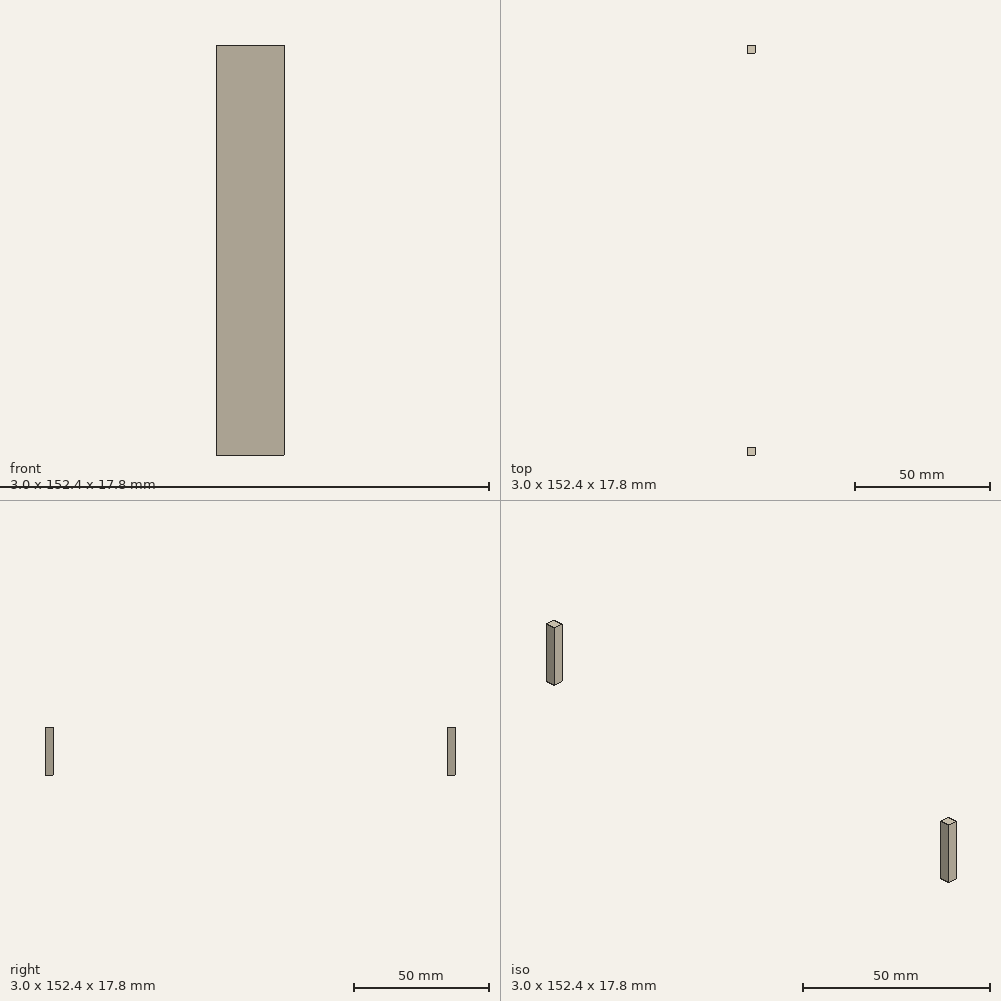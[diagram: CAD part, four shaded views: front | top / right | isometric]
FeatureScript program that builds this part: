
annotation { "Feature Type Name" : "Feature", "Feature Type Description" : "" }
export const myFeature = defineFeature(function(context is Context, id is Id, definition is map)
    precondition{}
    {
        {
            var Q0;
            Q0=qCreatedBy(makeId("Right.planeOp"),FACE);
            var sketch = newSketch(context, id + "F0", { "sketchPlane" : qUnion([Q0])});
            skLineSegment(sketch, "E0.bottom", {"start": v(76.2, -34.3) * mm, "end": v(-76.2, -34.3) * mm});
            skLineSegment(sketch, "E0.top", {"start": v(76.2, 34.3) * mm, "end": v(-76.2, 34.3) * mm});
            skLineSegment(sketch, "E0.left", {"start": v(76.2, -34.3) * mm, "end": v(76.2, 34.3) * mm});
            skLineSegment(sketch, "E0.right", {"start": v(-76.2, -34.3) * mm, "end": v(-76.2, 34.3) * mm});
            skPoint(sketch, "E0.middle", {"position": v(0, 0) * mm});
            skLineSegment(sketch, "E1.bottom", {"start": v(-76.2, -8.9) * mm, "end": v(-73.23, -8.9) * mm});
            skLineSegment(sketch, "E1.top", {"start": v(-76.2, -34.3) * mm, "end": v(-73.23, -34.3) * mm});
            skLineSegment(sketch, "E1.left", {"start": v(-76.2, -8.9) * mm, "end": v(-76.2, -34.3) * mm});
            skLineSegment(sketch, "E1.right", {"start": v(-73.23, -8.9) * mm, "end": v(-73.23, -34.3) * mm});
            skArc(sketch, "E2", {"start": v(-76.2, 2.57) * mm, "mid": v(-73.15, 3.8) * mm, "end": v(-76.2, 5.05) * mm});
            skLineSegment(sketch, "E3.bottom", {"start": v(-73.23, 34.3) * mm, "end": v(-76.2, 34.3) * mm});
            skLineSegment(sketch, "E3.top", {"start": v(-73.23, 16.51) * mm, "end": v(-76.2, 16.51) * mm});
            skLineSegment(sketch, "E3.left", {"start": v(-73.23, 34.3) * mm, "end": v(-73.23, 16.51) * mm});
            skLineSegment(sketch, "E3.right", {"start": v(-76.2, 34.3) * mm, "end": v(-76.2, 16.51) * mm});
            skLineSegment(sketch, "E4.MirrorCS", {"start": v(76.2, -34.3) * mm, "end": v(73.23, -34.3) * mm});
            skLineSegment(sketch, "E5.MirrorCS", {"start": v(73.23, 34.3) * mm, "end": v(76.2, 34.3) * mm});
            skLineSegment(sketch, "E6.MirrorCS", {"start": v(76.2, -8.9) * mm, "end": v(73.23, -8.9) * mm});
            skLineSegment(sketch, "E7.MirrorCS", {"start": v(73.23, 16.51) * mm, "end": v(76.2, 16.51) * mm});
            skArc(sketch, "E8.MirrorCS", {"start": v(76.2, 2.57) * mm, "mid": v(73.15, 3.8) * mm, "end": v(76.2, 5.05) * mm});
            skLineSegment(sketch, "E9.MirrorCS", {"start": v(73.23, -8.9) * mm, "end": v(73.23, -34.3) * mm});
            skLineSegment(sketch, "E10.MirrorCS", {"start": v(76.2, -8.9) * mm, "end": v(76.2, -34.3) * mm});
            skLineSegment(sketch, "E11.MirrorCS", {"start": v(76.2, 34.3) * mm, "end": v(76.2, 16.51) * mm});
            skLineSegment(sketch, "E12.MirrorCS", {"start": v(73.23, 34.3) * mm, "end": v(73.23, 16.51) * mm});
            skLineSegment(sketch, "E13.bottom", {"start": v(-76.2, -31.32) * mm, "end": v(-58.92, -31.32) * mm});
            skLineSegment(sketch, "E13.top", {"start": v(-76.2, -34.3) * mm, "end": v(-38.1, -34.3) * mm});
            skLineSegment(sketch, "E13.left", {"start": v(-76.2, -31.32) * mm, "end": v(-76.2, -34.3) * mm});
            skLineSegment(sketch, "E13.right", {"start": v(-38.1, -31.32) * mm, "end": v(-38.1, -34.3) * mm});
            skLineSegment(sketch, "E14.bottom", {"start": v(76.2, -31.32) * mm, "end": v(38.1, -31.32) * mm});
            skLineSegment(sketch, "E14.top", {"start": v(76.2, -34.3) * mm, "end": v(38.1, -34.3) * mm});
            skLineSegment(sketch, "E14.left", {"start": v(76.2, -31.32) * mm, "end": v(76.2, -34.3) * mm});
            skLineSegment(sketch, "E14.right", {"start": v(38.1, -31.32) * mm, "end": v(38.1, -34.3) * mm});
            skLineSegment(sketch, "E15.bottom", {"start": v(-12.7, -31.32) * mm, "end": v(12.7, -31.32) * mm});
            skLineSegment(sketch, "E15.top", {"start": v(-12.7, -34.3) * mm, "end": v(12.7, -34.3) * mm});
            skLineSegment(sketch, "E15.left", {"start": v(-12.7, -31.32) * mm, "end": v(-12.7, -34.3) * mm});
            skLineSegment(sketch, "E15.right", {"start": v(12.7, -31.32) * mm, "end": v(12.7, -34.3) * mm});
            skLineSegment(sketch, "E16.bottom", {"start": v(-58.92, -13.49) * mm, "end": v(-55.38, -13.49) * mm});
            skLineSegment(sketch, "E16.top", {"start": v(-58.92, -34.3) * mm, "end": v(-55.38, -34.3) * mm});
            skLineSegment(sketch, "E16.left", {"start": v(-58.92, -13.49) * mm, "end": v(-58.92, -18.52) * mm});
            skLineSegment(sketch, "E16.right", {"start": v(-55.38, -13.49) * mm, "end": v(-55.38, -18.52) * mm});
            skPoint(sketch, "E17", {"position": v(-57.15, -34.3) * mm});
            skLineSegment(sketch, "E18", {"start": v(-57.15, -34.3) * mm, "end": v(-57.15, -8.89) * mm, "construction": true});
            skPoint(sketch, "E18.endSnap0", {"position": v(-57.15, -13.49) * mm});
            skLineSegment(sketch, "E19.bottom", {"start": v(-53.26, -21.16) * mm, "end": v(-55.38, -21.16) * mm});
            skLineSegment(sketch, "E19.top", {"start": v(-53.26, -18.52) * mm, "end": v(-55.38, -18.52) * mm});
            skLineSegment(sketch, "E19.left", {"start": v(-53.26, -21.16) * mm, "end": v(-53.26, -18.52) * mm});
            skLineSegment(sketch, "E19.right", {"start": v(-61.04, -21.16) * mm, "end": v(-61.04, -18.52) * mm});
            skPoint(sketch, "E19.middle", {"position": v(-57.15, -19.84) * mm});
            skLineSegment(sketch, "E20.trimOffspring", {"start": v(-55.38, -31.32) * mm, "end": v(-38.1, -31.32) * mm});
            skLineSegment(sketch, "E21.trimOffspring", {"start": v(-55.38, -21.16) * mm, "end": v(-55.38, -31.32) * mm});
            skLineSegment(sketch, "E22.trimOffspring", {"start": v(-58.92, -18.52) * mm, "end": v(-61.04, -18.52) * mm});
            skLineSegment(sketch, "E23.trimOffspring", {"start": v(-58.92, -21.16) * mm, "end": v(-58.92, -31.32) * mm});
            skLineSegment(sketch, "E24.trimOffspring", {"start": v(-58.92, -21.16) * mm, "end": v(-61.04, -21.16) * mm});
            skLineSegment(sketch, "E25.1.0.0", {"start": v(61.04, -21.16) * mm, "end": v(61.04, -18.52) * mm});
            skLineSegment(sketch, "E25.1.0.1", {"start": v(61.04, -21.16) * mm, "end": v(58.92, -21.16) * mm});
            skPoint(sketch, "E25.1.0.2", {"position": v(57.15, -19.84) * mm});
            skLineSegment(sketch, "E25.1.0.3", {"start": v(55.38, -21.16) * mm, "end": v(53.26, -21.16) * mm});
            skLineSegment(sketch, "E25.1.0.4", {"start": v(58.92, -21.16) * mm, "end": v(58.92, -31.32) * mm});
            skLineSegment(sketch, "E25.1.0.5", {"start": v(53.26, -21.16) * mm, "end": v(53.26, -18.52) * mm});
            skLineSegment(sketch, "E25.1.0.6", {"start": v(55.38, -13.49) * mm, "end": v(58.92, -13.49) * mm});
            skLineSegment(sketch, "E25.1.0.7", {"start": v(55.38, -18.52) * mm, "end": v(53.26, -18.52) * mm});
            skLineSegment(sketch, "E25.1.0.8", {"start": v(55.38, -13.49) * mm, "end": v(55.38, -18.52) * mm});
            skPoint(sketch, "E25.1.0.9", {"position": v(57.15, -13.49) * mm});
            skLineSegment(sketch, "E25.1.0.10", {"start": v(61.04, -18.52) * mm, "end": v(58.92, -18.52) * mm});
            skLineSegment(sketch, "E25.1.0.11", {"start": v(55.38, -21.16) * mm, "end": v(55.38, -31.32) * mm});
            skLineSegment(sketch, "E25.1.0.12", {"start": v(58.92, -13.49) * mm, "end": v(58.92, -18.52) * mm});
            skLineSegment(sketch, "E25.direction1", {"start": v(-58.92, -31.32) * mm, "end": v(55.38, -31.32) * mm, "construction": true});
            skLineSegment(sketch, "E26.bottom", {"start": v(-1.77, -13.49) * mm, "end": v(1.77, -13.49) * mm});
            skLineSegment(sketch, "E26.top", {"start": v(-1.77, -34.3) * mm, "end": v(1.77, -34.3) * mm});
            skLineSegment(sketch, "E26.left", {"start": v(-1.77, -13.49) * mm, "end": v(-1.77, -18.52) * mm});
            skLineSegment(sketch, "E26.right", {"start": v(1.77, -13.49) * mm, "end": v(1.77, -18.52) * mm});
            skPoint(sketch, "E27", {"position": v(0, -34.3) * mm});
            skLineSegment(sketch, "E28.bottom", {"start": v(3.89, -21.16) * mm, "end": v(1.77, -21.16) * mm});
            skLineSegment(sketch, "E28.top", {"start": v(3.89, -18.52) * mm, "end": v(1.77, -18.52) * mm});
            skLineSegment(sketch, "E28.left", {"start": v(3.89, -21.16) * mm, "end": v(3.89, -18.52) * mm});
            skLineSegment(sketch, "E28.right", {"start": v(-3.89, -21.16) * mm, "end": v(-3.89, -18.52) * mm});
            skPoint(sketch, "E28.middle", {"position": v(0, -19.84) * mm});
            skLineSegment(sketch, "E29.trimOffspring", {"start": v(1.77, -21.16) * mm, "end": v(1.77, -31.32) * mm});
            skLineSegment(sketch, "E30.trimOffspring", {"start": v(-1.77, -18.52) * mm, "end": v(-3.89, -18.52) * mm});
            skLineSegment(sketch, "E31.trimOffspring", {"start": v(-1.77, -21.16) * mm, "end": v(-1.77, -31.32) * mm});
            skLineSegment(sketch, "E32.trimOffspring", {"start": v(-1.77, -21.16) * mm, "end": v(-3.89, -21.16) * mm});
            skSolve(sketch);
        }
        {
            var Q0;
            Q0=makeQuery(id+"F0.imprint","IMPRINT",FACE,{"disambiguationData":[TD([[makeQuery(id+"F0.imprint","IMPRINT",EDGE,{"derivedFrom":sQuery(id+"F0.wireOp",EDGE,"E0.top")}),1.0]])]});
            extrude(context, id + "F1", {"entities" : qUnion([Q0]), "depth" : 2.97 * mm});
        }
    });
